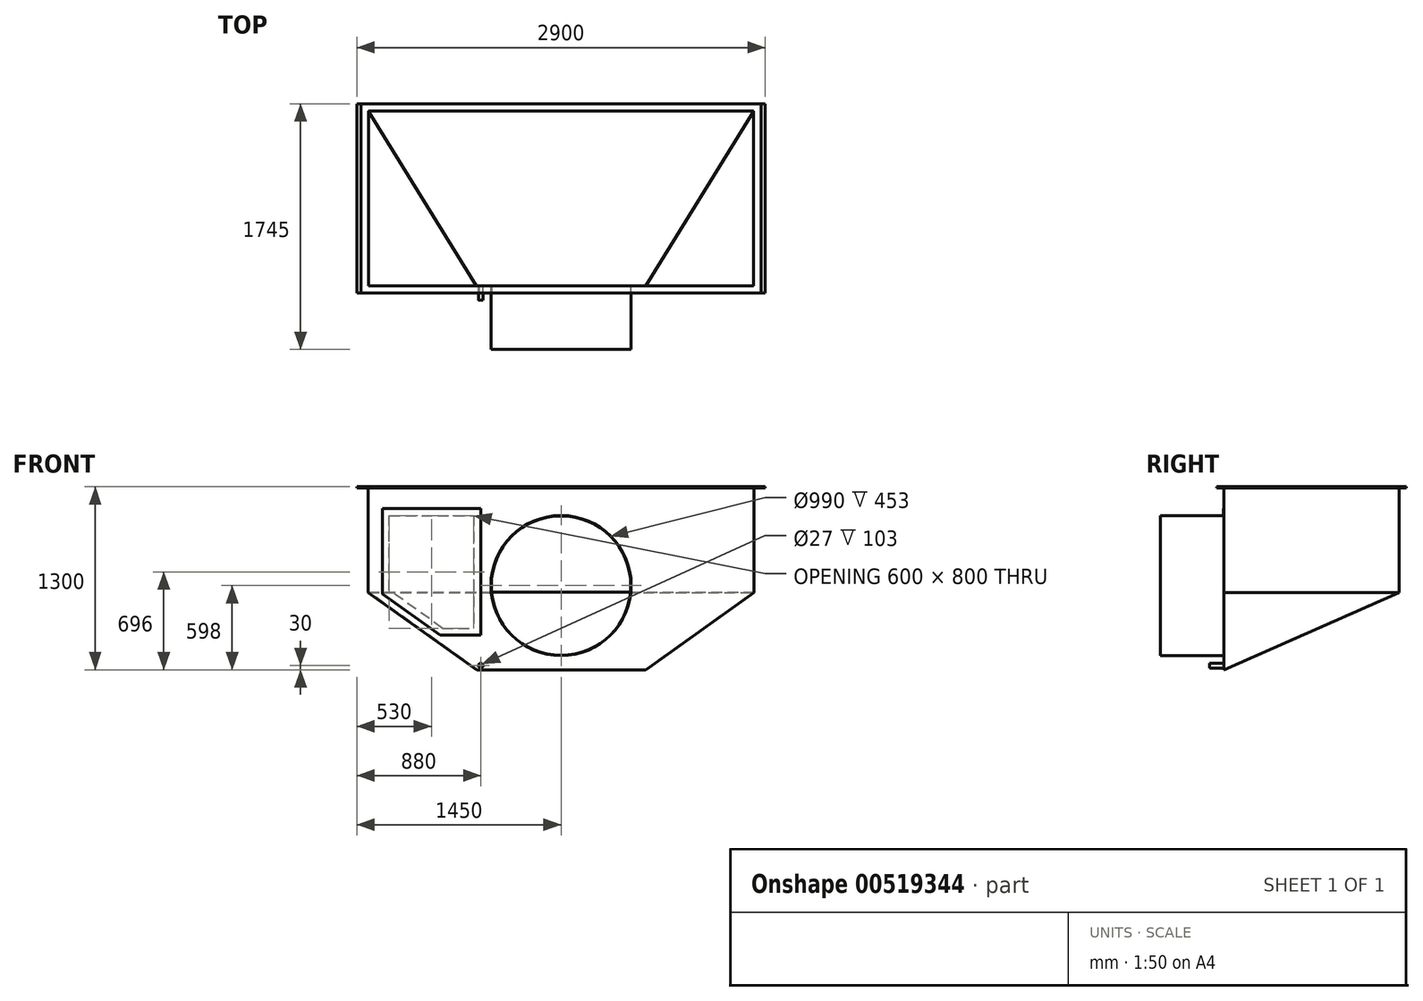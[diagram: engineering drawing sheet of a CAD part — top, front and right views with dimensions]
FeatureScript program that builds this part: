
annotation { "Feature Type Name" : "Feature", "Feature Type Description" : "" }
export const myFeature = defineFeature(function(context is Context, id is Id, definition is map)
    precondition{}
    {
        {
            var Q0;
            Q0=qCreatedBy(makeId("Top.planeOp"),FACE);
            var sketch = newSketch(context, id + "F0", { "sketchPlane" : qUnion([Q0])});
            skLineSegment(sketch, "E0.bottom", {"start": v(1367, 619.5) * mm, "end": v(-1367, 619.5) * mm});
            skLineSegment(sketch, "E0.top", {"start": v(1367, -619.5) * mm, "end": v(-1367, -619.5) * mm});
            skLineSegment(sketch, "E0.left", {"start": v(1367, 619.5) * mm, "end": v(1367, -619.5) * mm});
            skLineSegment(sketch, "E0.right", {"start": v(-1367, 619.5) * mm, "end": v(-1367, -619.5) * mm});
            skPoint(sketch, "E0.middle", {"position": v(0, 0) * mm});
            skLineSegment(sketch, "E1.bottom", {"start": v(1370, 622.5) * mm, "end": v(-1370, 622.5) * mm});
            skLineSegment(sketch, "E1.top", {"start": v(1370, -622.5) * mm, "end": v(-1370, -622.5) * mm});
            skLineSegment(sketch, "E1.left", {"start": v(1370, 622.5) * mm, "end": v(1370, -622.5) * mm});
            skLineSegment(sketch, "E1.right", {"start": v(-1370, 622.5) * mm, "end": v(-1370, -622.5) * mm});
            skSolve(sketch);
        }
        {
            var Q0;
            Q0 = qSketchRegion(id + "F0", true);
            extrude(context, id + "F1", {"entities" : qUnion([Q0]), "oppositeDirection" : true, "depth" : 1300 * mm, "offsetDistance" : 25 * mm});
        }
        {
            var Q0;
            Q0=qCreatedBy(makeId("Top.planeOp"),FACE);
            var sketch = newSketch(context, id + "F2", { "sketchPlane" : qUnion([Q0])});
            skLineSegment(sketch, "E2.0", {"start": v(1370, 622.5) * mm, "end": v(1370, -622.5) * mm});
            skLineSegment(sketch, "E3.0", {"start": v(1370, -622.5) * mm, "end": v(-1370, -622.5) * mm});
            skLineSegment(sketch, "E4.0", {"start": v(-1370, 622.5) * mm, "end": v(-1370, -622.5) * mm});
            skLineSegment(sketch, "E5.0", {"start": v(1370, 622.5) * mm, "end": v(-1370, 622.5) * mm});
            skLineSegment(sketch, "E6.bottom", {"start": v(1420, 672.5) * mm, "end": v(-1420, 672.5) * mm});
            skLineSegment(sketch, "E6.top", {"start": v(1420, -672.5) * mm, "end": v(-1420, -672.5) * mm});
            skLineSegment(sketch, "E6.left", {"start": v(1420, 672.5) * mm, "end": v(1420, -672.5) * mm});
            skLineSegment(sketch, "E6.right", {"start": v(-1420, 672.5) * mm, "end": v(-1420, -672.5) * mm});
            skPoint(sketch, "E6.middle", {"position": v(0, 0) * mm});
            skSolve(sketch);
        }
        {
            var Q0;
            Q0 = qSketchRegion(id + "F2", true);
            extrude(context, id + "F3", {"entities" : qUnion([Q0]), "operationType" : NewBodyOperationType.ADD, "oppositeDirection" : true, "depth" : 10 * mm, "offsetDistance" : 25 * mm});
        }
        {
            var Q0;
            Q0=makeQuery(id+"F1.opExtrude","SWEPT_FACE",FACE,{"disambiguationData":[OSD([sQuery(id+"F0.wireOp",EDGE,"E1.bottom")])]});
            var sketch = newSketch(context, id + "F4", { "sketchPlane" : qUnion([Q0])});
            skLineSegment(sketch, "E7", {"start": v(-1370, -750) * mm, "end": v(1370, -750) * mm, "construction": true});
            skSolve(sketch);
        }
        {
            var Q0;
            Q0=sQuery(id+"F4.wireOp",EDGE,"E7");
            var Q1;
            Q1=makeQuery(id+"F1.opExtrude","CAP_EDGE",EDGE,{"disambiguationData":[OSD([sQuery(id+"F0.wireOp",EDGE,"E1.top")])],"isStart":false});
            cPlane(context, id + "F5", {"entities" : qUnion([Q0, Q1]), "cplaneType" : CPlaneType.LINE_ANGLE, "offset" : 25 * mm, "angle" : 0 * degree, "width" : 150 * mm, "height" : 150 * mm});
        }
        {
            var Q0;
            Q0=qCreatedBy(id+"F5.planeOp",FACE);
            var sketch = newSketch(context, id + "F6", { "sketchPlane" : qUnion([Q0])});
            skLineSegment(sketch, "E8.bottom", {"start": v(1798.06, 1118.39) * mm, "end": v(-1958.57, 1118.39) * mm});
            skLineSegment(sketch, "E8.top", {"start": v(1798.06, -1692.2) * mm, "end": v(-1958.57, -1692.2) * mm});
            skLineSegment(sketch, "E8.left", {"start": v(1798.06, 1118.39) * mm, "end": v(1798.06, -1692.2) * mm});
            skLineSegment(sketch, "E8.right", {"start": v(-1958.57, 1118.39) * mm, "end": v(-1958.57, -1692.2) * mm});
            skSolve(sketch);
        }
        {
            var Q0;
            Q0=makeQuery(id+"F6.imprint","IMPRINT",FACE,{"disambiguationData":[TD([[makeQuery(id+"F6.imprint","IMPRINT",EDGE,{"derivedFrom":sQuery(id+"F6.wireOp",EDGE,"E8.bottom")}),1.0]])]});
            extrude(context, id + "F7", {"entities" : qUnion([Q0]), "operationType" : NewBodyOperationType.REMOVE, "endBound" : BoundingType.THROUGH_ALL, "oppositeDirection" : true, "depth" : 25 * mm, "offsetDistance" : 25 * mm});
        }
        {
            var Q0;
            Q0=qCreatedBy(id+"F5.planeOp",FACE);
            var sketch = newSketch(context, id + "F8", { "sketchPlane" : qUnion([Q0])});
            skLineSegment(sketch, "E9.0", {"start": v(1370, 266.34) * mm, "end": v(1370, 266.34) * mm});
            skLineSegment(sketch, "E10.0", {"start": v(-1370, 266.34) * mm, "end": v(-1370, 266.34) * mm});
            skLineSegment(sketch, "E11", {"start": v(1370, 266.34) * mm, "end": v(1370, 263.6) * mm});
            skLineSegment(sketch, "E12", {"start": v(-1370, 266.34) * mm, "end": v(-1370, 263.6) * mm});
            skLineSegment(sketch, "E13.0", {"start": v(-1370, -1094.73) * mm, "end": v(-1370, 266.34) * mm});
            skLineSegment(sketch, "E14.0", {"start": v(1370, -1094.73) * mm, "end": v(1370, 266.34) * mm});
            skLineSegment(sketch, "E15.0", {"start": v(-1370, 266.34) * mm, "end": v(1370, 266.34) * mm});
            skLineSegment(sketch, "E16.0", {"start": v(-1367, -1091.45) * mm, "end": v(1367, -1091.45) * mm});
            skLineSegment(sketch, "E17", {"start": v(-1367, -1091.45) * mm, "end": v(-1370, -1091.45) * mm});
            skLineSegment(sketch, "E18", {"start": v(1367, -1091.45) * mm, "end": v(1370, -1091.45) * mm});
            skSolve(sketch);
        }
        {
            var Q0;
            Q0 = qSketchRegion(id + "F8", true);
            extrude(context, id + "F9", {"entities" : qUnion([Q0]), "operationType" : NewBodyOperationType.ADD, "depth" : 3 * mm, "offsetDistance" : 25 * mm});
        }
        {
            var Q0;
            Q0=makeQuery(id+"F1.opExtrude","SWEPT_FACE",FACE,{"disambiguationData":[OSD([sQuery(id+"F0.wireOp",EDGE,"E1.right")])]});
            var sketch = newSketch(context, id + "F10", { "sketchPlane" : qUnion([Q0])});
            skLineSegment(sketch, "E19", {"start": v(-622.5, -750) * mm, "end": v(622.5, -750) * mm, "construction": true});
            skSolve(sketch);
        }
        {
            var Q0;
            Q0=makeQuery(id+"F1.opExtrude","SWEPT_FACE",FACE,{"disambiguationData":[OSD([sQuery(id+"F0.wireOp",EDGE,"E1.left")])]});
            var sketch = newSketch(context, id + "F11", { "sketchPlane" : qUnion([Q0])});
            skLineSegment(sketch, "E20", {"start": v(622.5, -750) * mm, "end": v(-622.5, -750) * mm, "construction": true});
            skSolve(sketch);
        }
        {
            var Q0;
            Q0=qCreatedBy(makeId("Top.planeOp"),FACE);
            cPlane(context, id + "F12", {"entities" : qUnion([Q0]), "cplaneType" : CPlaneType.OFFSET, "offset" : 1300 * mm, "oppositeDirection" : true, "width" : 150 * mm, "height" : 150 * mm});
        }
        {
            var Q0;
            Q0=qCreatedBy(id+"F12.planeOp",FACE);
            var sketch = newSketch(context, id + "F13", { "sketchPlane" : qUnion([Q0])});
            skLineSegment(sketch, "E21", {"start": v(0, 0) * mm, "end": v(0, -1369) * mm, "construction": true});
            skLineSegment(sketch, "E22.0", {"start": v(1420, -672.5) * mm, "end": v(-1420, -672.5) * mm, "construction": true});
            skLineSegment(sketch, "E23", {"start": v(-600, 1789.24) * mm, "end": v(-600, -2040.34) * mm, "construction": true});
            skLineSegment(sketch, "E24.MirrorCS", {"start": v(600, 1789.24) * mm, "end": v(600, -2040.34) * mm, "construction": true});
            skSolve(sketch);
        }
        {
            var Q0;
            Q0=sQuery(id+"F13.wireOp",EDGE,"E23");
            var Q1;
            Q1=sQuery(id+"F10.wireOp",EDGE,"E19");
            cPlane(context, id + "F14", {"entities" : qUnion([Q0, Q1]), "cplaneType" : CPlaneType.LINE_ANGLE, "offset" : 25 * mm, "angle" : 0 * degree, "width" : 150 * mm, "height" : 150 * mm});
        }
        {
            var Q0;
            Q0=qCreatedBy(id+"F14.planeOp",FACE);
            var sketch = newSketch(context, id + "F15", { "sketchPlane" : qUnion([Q0])});
            skLineSegment(sketch, "E25.bottom", {"start": v(-2436.47, -2780.34) * mm, "end": v(3144.7, -2780.34) * mm});
            skLineSegment(sketch, "E25.top", {"start": v(-2436.47, 3069.12) * mm, "end": v(3144.7, 3069.12) * mm});
            skLineSegment(sketch, "E25.left", {"start": v(-2436.47, -2780.34) * mm, "end": v(-2436.47, 3069.12) * mm});
            skLineSegment(sketch, "E25.right", {"start": v(3144.7, -2780.34) * mm, "end": v(3144.7, 3069.12) * mm});
            skSolve(sketch);
        }
        {
            var Q0;
            Q0 = qSketchRegion(id + "F15", true);
            extrude(context, id + "F16", {"entities" : qUnion([Q0]), "operationType" : NewBodyOperationType.REMOVE, "endBound" : BoundingType.THROUGH_ALL, "depth" : 25 * mm, "offsetDistance" : 25 * mm});
        }
        {
            var Q0;
            Q0=sQuery(id+"F13.wireOp",EDGE,"E24.MirrorCS");
            var Q1;
            Q1=sQuery(id+"F11.wireOp",EDGE,"E20");
            cPlane(context, id + "F17", {"entities" : qUnion([Q0, Q1]), "cplaneType" : CPlaneType.LINE_ANGLE, "offset" : 25 * mm, "angle" : 0 * degree, "oppositeDirection" : true, "width" : 150 * mm, "height" : 150 * mm});
        }
        {
            var Q0;
            Q0=qCreatedBy(id+"F17.planeOp",FACE);
            var sketch = newSketch(context, id + "F18", { "sketchPlane" : qUnion([Q0])});
            skLineSegment(sketch, "E26.bottom", {"start": v(-2725.2, 2875.07) * mm, "end": v(2428.52, 2875.07) * mm});
            skLineSegment(sketch, "E26.top", {"start": v(-2725.2, -2707.87) * mm, "end": v(2428.52, -2707.87) * mm});
            skLineSegment(sketch, "E26.left", {"start": v(-2725.2, 2875.07) * mm, "end": v(-2725.2, -2707.87) * mm});
            skLineSegment(sketch, "E26.right", {"start": v(2428.52, 2875.07) * mm, "end": v(2428.52, -2707.87) * mm});
            skSolve(sketch);
        }
        {
            var Q0;
            Q0 = qSketchRegion(id + "F18", true);
            extrude(context, id + "F19", {"entities" : qUnion([Q0]), "operationType" : NewBodyOperationType.REMOVE, "endBound" : BoundingType.THROUGH_ALL, "oppositeDirection" : true, "depth" : 25 * mm, "offsetDistance" : 25 * mm});
        }
        {
            var Q0;
            Q0=qCreatedBy(id+"F14.planeOp",FACE);
            var sketch = newSketch(context, id + "F20", { "sketchPlane" : qUnion([Q0])});
            skLineSegment(sketch, "E27.0", {"start": v(-678.89, -622.5) * mm, "end": v(-678.89, 622.5) * mm});
            skLineSegment(sketch, "E28.0", {"start": v(-678.89, -622.5) * mm, "end": v(267.37, 622.5) * mm});
            skLineSegment(sketch, "E29.0", {"start": v(267.37, 622.5) * mm, "end": v(-678.89, 622.5) * mm});
            skSolve(sketch);
        }
        {
            var Q0;
            Q0 = qSketchRegion(id + "F20", true);
            extrude(context, id + "F21", {"entities" : qUnion([Q0]), "operationType" : NewBodyOperationType.ADD, "oppositeDirection" : true, "depth" : 3 * mm, "offsetDistance" : 25 * mm});
        }
        {
            var Q0;
            Q0=qCreatedBy(id+"F17.planeOp",FACE);
            var sketch = newSketch(context, id + "F22", { "sketchPlane" : qUnion([Q0])});
            skLineSegment(sketch, "E30.0", {"start": v(678.89, -622.5) * mm, "end": v(678.89, 622.5) * mm});
            skLineSegment(sketch, "E31.0", {"start": v(-267.37, -622.5) * mm, "end": v(678.89, -622.5) * mm});
            skLineSegment(sketch, "E32.0", {"start": v(678.89, 622.5) * mm, "end": v(-267.37, -622.5) * mm});
            skSolve(sketch);
        }
        {
            var Q0;
            Q0 = qSketchRegion(id + "F22", true);
            extrude(context, id + "F23", {"entities" : qUnion([Q0]), "operationType" : NewBodyOperationType.ADD, "depth" : 3 * mm, "offsetDistance" : 25 * mm});
        }
        {
            var Q0;
            Q0=makeQuery(id+"F1.opExtrude","SWEPT_FACE",FACE,{"disambiguationData":[OSD([sQuery(id+"F0.wireOp",EDGE,"E1.top")])]});
            var sketch = newSketch(context, id + "F24", { "sketchPlane" : qUnion([Q0])});
            skLineSegment(sketch, "E33", {"start": v(0, 0) * mm, "end": v(0, -1659.43) * mm, "construction": true});
            skPoint(sketch, "E33.endSnap0", {"position": v(0, -1300) * mm});
            skCircle(sketch, "E34", {"center": v(0, -702) * mm, "radius": 495 * mm});
            skSolve(sketch);
        }
        {
            var Q0;
            Q0 = qSketchRegion(id + "F24", true);
            extrude(context, id + "F25", {"entities" : qUnion([Q0]), "operationType" : NewBodyOperationType.REMOVE, "oppositeDirection" : true, "depth" : 25 * mm, "offsetDistance" : 25 * mm});
        }
        {
            var Q0;
            Q0=makeQuery(id+"F1.opExtrude","SWEPT_FACE",FACE,{"disambiguationData":[OSD([sQuery(id+"F0.wireOp",EDGE,"E1.top")])]});
            var sketch = newSketch(context, id + "F26", { "sketchPlane" : qUnion([Q0])});
            skCircle(sketch, "E35.0", {"center": v(0, -702) * mm, "radius": 495 * mm});
            skCircle(sketch, "E36", {"center": v(0, -702) * mm, "radius": 498 * mm});
            skSolve(sketch);
        }
        {
            var Q0;
            Q0 = qSketchRegion(id + "F26", true);
            extrude(context, id + "F27", {"entities" : qUnion([Q0]), "operationType" : NewBodyOperationType.ADD, "depth" : 450 * mm, "offsetDistance" : 25 * mm});
        }
        {
            var Q0;
            Q0=makeQuery(id+"F1.opExtrude","SWEPT_FACE",FACE,{"disambiguationData":[OSD([sQuery(id+"F0.wireOp",EDGE,"E1.top")])]});
            var sketch = newSketch(context, id + "F28", { "sketchPlane" : qUnion([Q0])});
            skLineSegment(sketch, "E37", {"start": v(0, -204) * mm, "end": v(-1778.5, -204) * mm, "construction": true});
            skLineSegment(sketch, "E38", {"start": v(-1220, -204) * mm, "end": v(-1220, -734.25) * mm});
            skLineSegment(sketch, "E39", {"start": v(-1220, -734.25) * mm, "end": v(-842.35, -1004) * mm});
            skLineSegment(sketch, "E40", {"start": v(-620, -1004) * mm, "end": v(-620, -204) * mm});
            skLineSegment(sketch, "E41", {"start": v(-620, -204) * mm, "end": v(-1220, -204) * mm});
            skLineSegment(sketch, "E42", {"start": v(-525.6, -1004) * mm, "end": v(-1750.28, -1004) * mm, "construction": true});
            skLineSegment(sketch, "E43", {"start": v(-620, -1004) * mm, "end": v(-842.35, -1004) * mm});
            skSolve(sketch);
        }
        {
            var Q0;
            Q0 = qSketchRegion(id + "F28", true);
            extrude(context, id + "F29", {"entities" : qUnion([Q0]), "operationType" : NewBodyOperationType.REMOVE, "oppositeDirection" : true, "depth" : 25 * mm, "offsetDistance" : 25 * mm});
        }
        {
            var Q0;
            Q0=makeQuery(id+"F1.opExtrude","SWEPT_FACE",FACE,{"disambiguationData":[OSD([sQuery(id+"F0.wireOp",EDGE,"E1.top")])]});
            var sketch = newSketch(context, id + "F30", { "sketchPlane" : qUnion([Q0])});
            skCircle(sketch, "E44", {"center": v(-570, -1270) * mm, "radius": 13.5 * mm});
            skSolve(sketch);
        }
        {
            var Q0;
            Q0 = qSketchRegion(id + "F30", true);
            extrude(context, id + "F31", {"entities" : qUnion([Q0]), "operationType" : NewBodyOperationType.REMOVE, "oppositeDirection" : true, "depth" : 3 * mm, "offsetDistance" : 25 * mm});
        }
        {
            var Q0;
            Q0=makeQuery(id+"F1.opExtrude","SWEPT_FACE",FACE,{"disambiguationData":[OSD([sQuery(id+"F0.wireOp",EDGE,"E1.top")])]});
            var sketch = newSketch(context, id + "F32", { "sketchPlane" : qUnion([Q0])});
            skCircle(sketch, "E45.0", {"center": v(-570, -1270) * mm, "radius": 13.5 * mm});
            skCircle(sketch, "E46", {"center": v(-570, -1270) * mm, "radius": 16.5 * mm});
            skSolve(sketch);
        }
        {
            var Q0;
            Q0 = qSketchRegion(id + "F32", true);
            extrude(context, id + "F33", {"entities" : qUnion([Q0]), "operationType" : NewBodyOperationType.ADD, "depth" : 100 * mm, "offsetDistance" : 25 * mm});
        }
        {
            var Q0;
            Q0=makeQuery(id+"F1.opExtrude","SWEPT_FACE",FACE,{"disambiguationData":[OSD([sQuery(id+"F0.wireOp",EDGE,"E1.top")])]});
            var sketch = newSketch(context, id + "F34", { "sketchPlane" : qUnion([Q0])});
            skLineSegment(sketch, "E47.0", {"start": v(-1270, -759.98) * mm, "end": v(-858.38, -1054) * mm});
            skLineSegment(sketch, "E47.1", {"start": v(-1270, -154) * mm, "end": v(-1270, -759.98) * mm});
            skLineSegment(sketch, "E47.2", {"start": v(-570, -1054) * mm, "end": v(-858.38, -1054) * mm});
            skLineSegment(sketch, "E47.3", {"start": v(-570, -1054) * mm, "end": v(-570, -154) * mm});
            skLineSegment(sketch, "E47.4", {"start": v(-570, -154) * mm, "end": v(-1270, -154) * mm});
            skSolve(sketch);
        }
        {
            var Q0;
            Q0 = qSketchRegion(id + "F34", true);
            extrude(context, id + "F35", {"entities" : qUnion([Q0]), "depth" : 3 * mm, "offsetDistance" : 25 * mm});
        }
        {
            var Q0;
            Q0=makeQuery(id+"F3.boolean.opBoolean","MERGE",FACE,{"derivedFrom":[makeQuery(id+"F1.opExtrude","CAP_FACE",FACE,{"disambiguationData":[OSD([sQuery(id+"F0.wireOp",EDGE,"E0.bottom"),sQuery(id+"F0.wireOp",EDGE,"E0.top"),sQuery(id+"F0.wireOp",EDGE,"E0.left"),sQuery(id+"F0.wireOp",EDGE,"E0.right"),sQuery(id+"F0.wireOp",EDGE,"E1.bottom"),sQuery(id+"F0.wireOp",EDGE,"E1.top"),sQuery(id+"F0.wireOp",EDGE,"E1.left"),sQuery(id+"F0.wireOp",EDGE,"E1.right")])],"isStart":true}),makeQuery(id+"F3.opExtrude","CAP_FACE",FACE,{"disambiguationData":[OSD([sQuery(id+"F2.wireOp",EDGE,"E2.0"),sQuery(id+"F2.wireOp",EDGE,"E3.0"),sQuery(id+"F2.wireOp",EDGE,"E4.0"),sQuery(id+"F2.wireOp",EDGE,"E5.0"),sQuery(id+"F2.wireOp",EDGE,"E6.bottom"),sQuery(id+"F2.wireOp",EDGE,"E6.top"),sQuery(id+"F2.wireOp",EDGE,"E6.left"),sQuery(id+"F2.wireOp",EDGE,"E6.right")])],"isStart":true})]});
            var sketch = newSketch(context, id + "F36", { "sketchPlane" : qUnion([Q0])});
            skLineSegment(sketch, "E48.0", {"start": v(-1420, 672.5) * mm, "end": v(-1420, -672.5) * mm});
            skLineSegment(sketch, "E49.bottom", {"start": v(-1420, 672.5) * mm, "end": v(-1450, 672.5) * mm});
            skLineSegment(sketch, "E49.top", {"start": v(-1420, -672.5) * mm, "end": v(-1450, -672.5) * mm});
            skLineSegment(sketch, "E49.right", {"start": v(-1450, 672.5) * mm, "end": v(-1450, -672.5) * mm});
            skLineSegment(sketch, "E50", {"start": v(0, 0) * mm, "end": v(0, 1010.91) * mm, "construction": true});
            skLineSegment(sketch, "E51.MirrorCS", {"start": v(1420, 672.5) * mm, "end": v(1450, 672.5) * mm});
            skLineSegment(sketch, "E52.MirrorCS", {"start": v(1420, -672.5) * mm, "end": v(1450, -672.5) * mm});
            skLineSegment(sketch, "E53.MirrorCS", {"start": v(1420, 672.5) * mm, "end": v(1420, -672.5) * mm});
            skLineSegment(sketch, "E54.MirrorCS", {"start": v(1450, 672.5) * mm, "end": v(1450, -672.5) * mm});
            skSolve(sketch);
        }
        {
            var Q0;
            Q0 = qSketchRegion(id + "F36", true);
            extrude(context, id + "F37", {"entities" : qUnion([Q0]), "oppositeDirection" : true, "depth" : 10 * mm, "offsetDistance" : 25 * mm});
        }
    });
